FCSTD DOCUMENT  (FreeCAD 0.19R24267 +148 (Git))
Label: Grundlage
License: All rights reserved
LicenseURL: http://en.wikipedia.org/wiki/All_rights_reserved
objects: Sketcher::SketchObject×1, PartDesign::Body×1
note: 2 computed .brp shape members not serialized (recipe doc carries the construction recipe); baked Part::Feature solids carry a one-line shape summary decoded from their .brp

FEATURE [Sketcher::SketchObject] Sketch
  FullyConstrained = true
  MapMode = 5
  Support = -> [XY_Plane]
  sketch-geometry (9):
    g0: LineSegment StartX=0 StartY=0 StartZ=0 EndX=94 EndY=0 EndZ=0
    g1: LineSegment StartX=94 StartY=0 StartZ=0 EndX=94 EndY=68.7 EndZ=0
    g2: LineSegment StartX=94 StartY=68.7 StartZ=0 EndX=0 EndY=68.7 EndZ=0
    g3: LineSegment StartX=0 StartY=68.7 StartZ=0 EndX=0 EndY=0 EndZ=0
    g4: GeomPoint X=47 Y=34.35 Z=0
    g5: Circle CenterX=3.45 CenterY=65.25 CenterZ=0 NormalX=0 NormalY=0 NormalZ=1 AngleXU=0 Radius=1.6
    g6: Circle CenterX=90.55 CenterY=65.25 CenterZ=0 NormalX=0 NormalY=0 NormalZ=1 AngleXU=0 Radius=1.6
    g7: Circle CenterX=90.55 CenterY=3.45 CenterZ=0 NormalX=0 NormalY=0 NormalZ=1 AngleXU=0 Radius=1.6
    g8: Circle CenterX=3.45 CenterY=3.45 CenterZ=0 NormalX=0 NormalY=0 NormalZ=1 AngleXU=0 Radius=1.6
  constraints (22):
    c: Coincident(g0,g1)
    c: Coincident(g1,g2)
    c: Coincident(g2,g3)
    c: Coincident(g3,g0)
    c: Horizontal(g0)
    c: Horizontal(g2)
    c: Vertical(g1)
    c: Vertical(g3)
    c: Coincident(g0,g-1)
    c: DistanceX(g2,g2) = 94
    c: DistanceY(g3,g3) = 68.7
    c: Symmetric(g2,g0,g4)
    c: Equal(g8,g5)
    c: Equal(g5,g6)
    c: Equal(g6,g7)
    c: Symmetric(g8,g6,g4)
    c: Symmetric(g5,g7,g4)
    c: Radius(g7) = 1.6
    c: Vertical(g8,g5)
    c: Horizontal(g8,g7)
    c: DistanceY(g0,g8) = 3.45
    c: DistanceX(g0,g8) = 3.45
FEATURE [PartDesign::Body] Body
  Group = -> [Sketch]
  Origin = -> Origin
